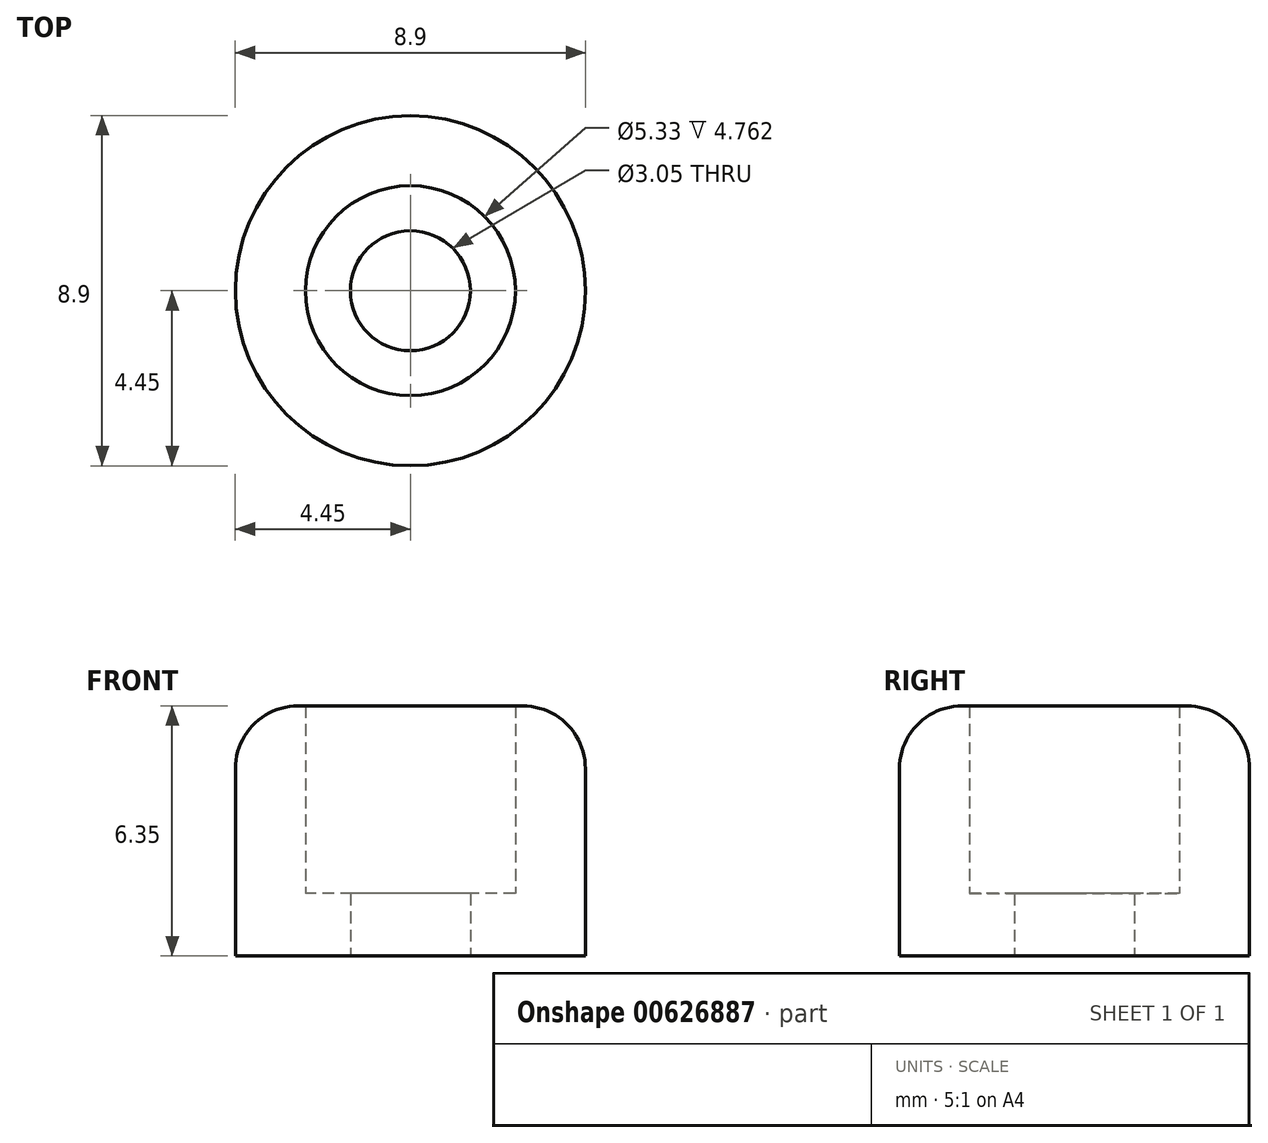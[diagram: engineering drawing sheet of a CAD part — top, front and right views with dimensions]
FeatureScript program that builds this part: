
annotation { "Feature Type Name" : "Feature", "Feature Type Description" : "" }
export const myFeature = defineFeature(function(context is Context, id is Id, definition is map)
    precondition{}
    {
        {
            var Q0;
            Q0=qCreatedBy(makeId("Top.planeOp"),FACE);
            var sketch = newSketch(context, id + "F0", { "sketchPlane" : qUnion([Q0])});
            skCircle(sketch, "E0", {"center": v(0, 0) * mm, "radius": 2.67 * mm});
            skCircle(sketch, "E1", {"center": v(0, 0) * mm, "radius": 1.52 * mm});
            skCircle(sketch, "E2", {"center": v(0, 0) * mm, "radius": 4.45 * mm});
            skSolve(sketch);
        }
        {
            var Q0;
            Q0=makeQuery(id+"F0.imprint","IMPRINT",FACE,{"disambiguationData":[TD([[makeQuery(id+"F0.imprint","IMPRINT",EDGE,{"derivedFrom":sQuery(id+"F0.wireOp",EDGE,"E0")}),-1.0]])]});
            extrude(context, id + "F1", {"entities" : qUnion([Q0]), "depth" : 6.35 * mm, "offsetDistance" : 25.4 * mm});
        }
        {
            var Q0;
            Q0=makeQuery(id+"F0.imprint","IMPRINT",FACE,{"disambiguationData":[TD([[makeQuery(id+"F0.imprint","IMPRINT",EDGE,{"derivedFrom":sQuery(id+"F0.wireOp",EDGE,"E0")}),1.0]])]});
            extrude(context, id + "F2", {"entities" : qUnion([Q0]), "operationType" : NewBodyOperationType.ADD, "depth" : 1.59 * mm, "offsetDistance" : 25.4 * mm});
        }
        {
            var Q0;
            Q0=makeQuery(id+"F1.opExtrude","CAP_EDGE",EDGE,{"disambiguationData":[OSD([sQuery(id+"F0.wireOp",EDGE,"E2")])],"isStart":false});
            fillet(context, id + "F3", {"entities" : qUnion([Q0]), "radius" : 1.59 * mm, "tangentPropagation" : true, "allowEdgeOverflow" : false});
        }
    });
